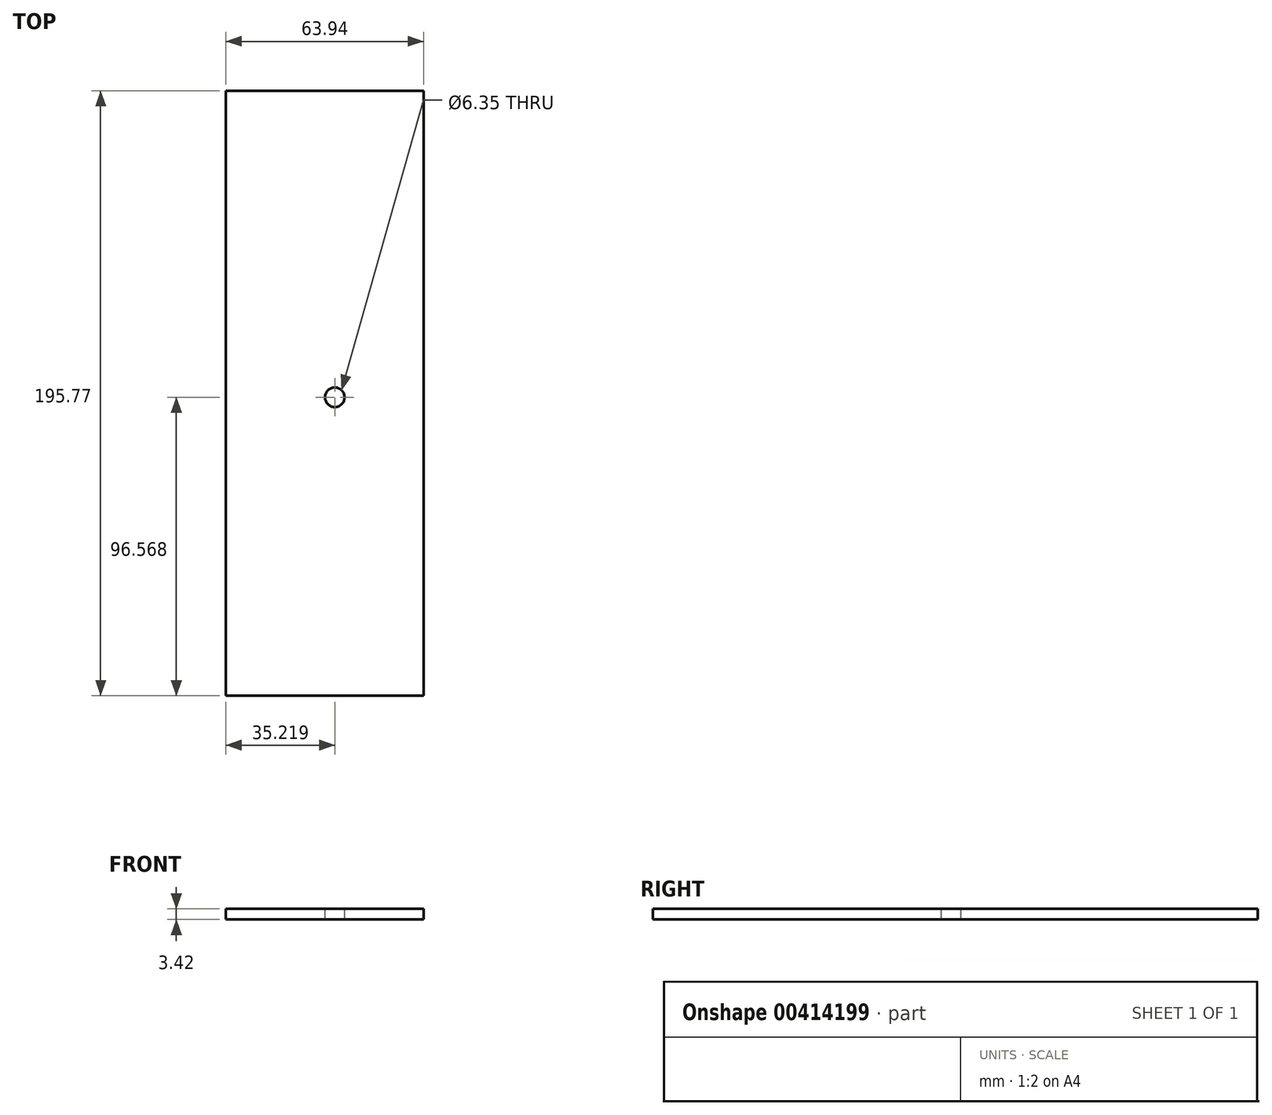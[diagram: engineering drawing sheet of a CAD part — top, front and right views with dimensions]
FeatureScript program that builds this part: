
annotation { "Feature Type Name" : "Feature", "Feature Type Description" : "" }
export const myFeature = defineFeature(function(context is Context, id is Id, definition is map)
    precondition{}
    {
        {
            var Q0;
            Q0=qCreatedBy(makeId("Top.planeOp"),FACE);
            var sketch = newSketch(context, id + "F0", { "sketchPlane" : qUnion([Q0])});
            skLineSegment(sketch, "E0.bottom", {"start": v(10.37, 88.14) * mm, "end": v(-53.57, 88.14) * mm});
            skLineSegment(sketch, "E0.top", {"start": v(10.37, -107.63) * mm, "end": v(-53.57, -107.63) * mm});
            skLineSegment(sketch, "E0.left", {"start": v(10.37, 88.14) * mm, "end": v(10.37, -107.63) * mm});
            skLineSegment(sketch, "E0.right", {"start": v(-53.57, 88.14) * mm, "end": v(-53.57, -107.63) * mm});
            skSolve(sketch);
        }
        {
            var Q0;
            Q0=makeQuery(id+"F0.imprint","IMPRINT",FACE,{"disambiguationData":[TD([[makeQuery(id+"F0.imprint","IMPRINT",EDGE,{"derivedFrom":sQuery(id+"F0.wireOp",EDGE,"E0.bottom")}),1.0]])]});
            var Q1;
            Q1 = qSketchRegion(id + "F0", true);
            extrude(context, id + "F1", {"entities" : qUnion([Q0, Q1]), "depth" : 3.42 * mm});
        }
        {
            var Q0;
            Q0=makeQuery(id+"F1.opExtrude","CAP_FACE",FACE,{"disambiguationData":[OSD([sQuery(id+"F0.wireOp",EDGE,"E0.bottom"),sQuery(id+"F0.wireOp",EDGE,"E0.top"),sQuery(id+"F0.wireOp",EDGE,"E0.left"),sQuery(id+"F0.wireOp",EDGE,"E0.right")])],"isStart":false});
            var sketch = newSketch(context, id + "F2", { "sketchPlane" : qUnion([Q0])});
            skCircle(sketch, "E1", {"center": v(-18.35, -11.06) * mm, "radius": 21.43 * mm});
            skSolve(sketch);
        }
        {
            var Q0;
            Q0=sQuery(id+"F2.wireOp",VERTEX,"E1.center");
            var Q1;
            Q1=makeQuery(id+"F1.opExtrude","SWEPT_BODY",BODY,{"disambiguationData":[OSD([sQuery(id+"F0.wireOp",EDGE,"E0.bottom"),sQuery(id+"F0.wireOp",EDGE,"E0.top"),sQuery(id+"F0.wireOp",EDGE,"E0.left"),sQuery(id+"F0.wireOp",EDGE,"E0.right")])]});
            hole(context, id + "F3", {"style" : HoleStyle.SIMPLE, "endStyle" : HoleEndStyle.THROUGH, "holeDiameter" : 6.35 * mm, "isTappedThrough" : true, "tappedDepth" : 12.7 * mm, "tapClearance" : 3, "locations" : qUnion([Q0]), "scope" : qUnion([Q1])});
        }
    });
